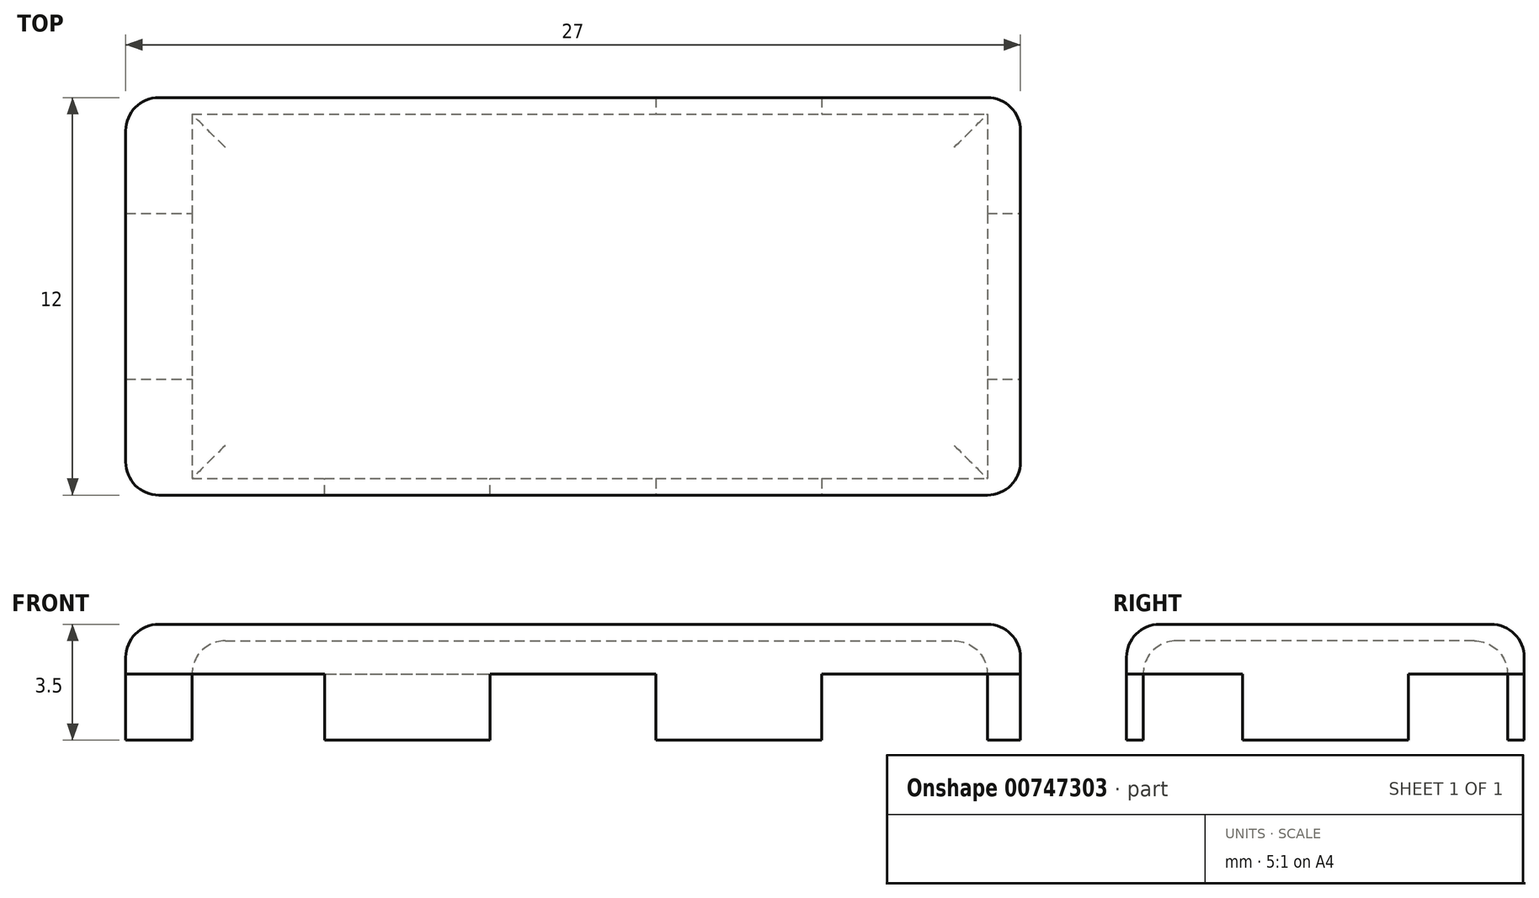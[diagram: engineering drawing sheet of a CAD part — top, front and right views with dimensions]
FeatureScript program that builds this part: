
annotation { "Feature Type Name" : "Feature", "Feature Type Description" : "" }
export const myFeature = defineFeature(function(context is Context, id is Id, definition is map)
    precondition{}
    {
        {
            var Q0;
            Q0=qCreatedBy(makeId("Top.planeOp"),FACE);
            var sketch = newSketch(context, id + "F0", { "sketchPlane" : qUnion([Q0])});
            skLineSegment(sketch, "E0.bottom", {"start": v(1, 0) * mm, "end": v(26, 0) * mm});
            skLineSegment(sketch, "E0.top", {"start": v(1, 12) * mm, "end": v(26, 12) * mm});
            skLineSegment(sketch, "E0.left", {"start": v(0, 1) * mm, "end": v(0, 11) * mm});
            skLineSegment(sketch, "E0.right", {"start": v(27, 1) * mm, "end": v(27, 11) * mm});
            skPoint(sketch, "E1.visualSharp", {"position": v(27, 12) * mm});
            skArc(sketch, "E1.filletArc", {"start": v(27, 11) * mm, "mid": v(26.7, 11.7) * mm, "end": v(26, 12) * mm});
            skPoint(sketch, "E2.visualSharp", {"position": v(27, 0) * mm});
            skArc(sketch, "E2.filletArc", {"start": v(26, 0) * mm, "mid": v(26.7, 0.3) * mm, "end": v(27, 1) * mm});
            skPoint(sketch, "E3.visualSharp", {"position": v(0, 0) * mm});
            skArc(sketch, "E3.filletArc", {"start": v(0, 1) * mm, "mid": v(0.3, 0.3) * mm, "end": v(1, 0) * mm});
            skPoint(sketch, "E4.visualSharp", {"position": v(0, 12) * mm});
            skArc(sketch, "E4.filletArc", {"start": v(1, 12) * mm, "mid": v(0.3, 11.7) * mm, "end": v(0, 11) * mm});
            skSolve(sketch);
        }
        {
            var Q0;
            Q0=makeQuery(id+"F0.imprint","IMPRINT",FACE,{"disambiguationData":[TD([[makeQuery(id+"F0.imprint","IMPRINT",EDGE,{"derivedFrom":sQuery(id+"F0.wireOp",EDGE,"E0.bottom")}),1.0]])]});
            extrude(context, id + "F1", {"entities" : qUnion([Q0]), "depth" : 1.5 * mm, "offsetDistance" : 25 * mm});
        }
        {
            var Q0;
            Q0=makeQuery(id+"F1.opExtrude","CAP_FACE",FACE,{"disambiguationData":[OSD([sQuery(id+"F0.wireOp",EDGE,"E0.bottom"),sQuery(id+"F0.wireOp",EDGE,"E0.top"),sQuery(id+"F0.wireOp",EDGE,"E0.left"),sQuery(id+"F0.wireOp",EDGE,"E0.right"),sQuery(id+"F0.wireOp",EDGE,"E1.filletArc"),sQuery(id+"F0.wireOp",EDGE,"E2.filletArc"),sQuery(id+"F0.wireOp",EDGE,"E3.filletArc"),sQuery(id+"F0.wireOp",EDGE,"E4.filletArc")])],"isStart":false});
            fillet(context, id + "F2", {"entities" : qUnion([Q0]), "radius" : 1 * mm, "tangentPropagation" : true, "allowEdgeOverflow" : false});
        }
        {
            var Q0;
            Q0=qCreatedBy(makeId("Top.planeOp"),FACE);
            var sketch = newSketch(context, id + "F3", { "sketchPlane" : qUnion([Q0])});
            skLineSegment(sketch, "E5.bottom", {"start": v(2, 11.5) * mm, "end": v(26, 11.5) * mm});
            skLineSegment(sketch, "E5.top", {"start": v(2, 0.5) * mm, "end": v(26, 0.5) * mm});
            skLineSegment(sketch, "E5.left", {"start": v(2, 11.5) * mm, "end": v(2, 0.5) * mm});
            skLineSegment(sketch, "E5.right", {"start": v(26, 11.5) * mm, "end": v(26, 0.5) * mm});
            skSolve(sketch);
        }
        {
            var Q0;
            Q0=qSketchRegion(id+"F3",true);
            extrude(context, id + "F4", {"entities" : qUnion([Q0]), "operationType" : NewBodyOperationType.REMOVE, "depth" : 1 * mm, "offsetDistance" : 25 * mm});
        }
        {
            var Q0;
            Q0=makeQuery(id+"F4.boolean.opBoolean","COPY",FACE,{"derivedFrom":makeQuery(id+"F4.opExtrude","CAP_FACE",FACE,{"disambiguationData":[OSD([sQuery(id+"F3.wireOp",EDGE,"E5.bottom"),sQuery(id+"F3.wireOp",EDGE,"E5.top"),sQuery(id+"F3.wireOp",EDGE,"E5.left"),sQuery(id+"F3.wireOp",EDGE,"E5.right")])],"isStart":false})});
            fillet(context, id + "F5", {"entities" : qUnion([Q0]), "radius" : 1 * mm, "tangentPropagation" : true, "allowEdgeOverflow" : false});
        }
        {
            var Q0;
            Q0=makeQuery(id+"F1.opExtrude","CAP_FACE",FACE,{"disambiguationData":[OSD([sQuery(id+"F0.wireOp",EDGE,"E0.bottom"),sQuery(id+"F0.wireOp",EDGE,"E0.top"),sQuery(id+"F0.wireOp",EDGE,"E0.left"),sQuery(id+"F0.wireOp",EDGE,"E0.right"),sQuery(id+"F0.wireOp",EDGE,"E1.filletArc"),sQuery(id+"F0.wireOp",EDGE,"E2.filletArc"),sQuery(id+"F0.wireOp",EDGE,"E3.filletArc"),sQuery(id+"F0.wireOp",EDGE,"E4.filletArc")])],"isStart":true});
            var sketch = newSketch(context, id + "F6", { "sketchPlane" : qUnion([Q0])});
            skLineSegment(sketch, "E6.bottom", {"start": v(0, -3.5) * mm, "end": v(2, -3.5) * mm});
            skLineSegment(sketch, "E6.top", {"start": v(0, -8.5) * mm, "end": v(2, -8.5) * mm});
            skLineSegment(sketch, "E6.left", {"start": v(0, -3.5) * mm, "end": v(0, -8.5) * mm});
            skLineSegment(sketch, "E6.right", {"start": v(2, -3.5) * mm, "end": v(2, -8.5) * mm});
            skLineSegment(sketch, "E7.bottom", {"start": v(26, -8.5) * mm, "end": v(27, -8.5) * mm});
            skLineSegment(sketch, "E7.top", {"start": v(26, -3.5) * mm, "end": v(27, -3.5) * mm});
            skLineSegment(sketch, "E7.left", {"start": v(26, -8.5) * mm, "end": v(26, -3.5) * mm});
            skLineSegment(sketch, "E7.right", {"start": v(27, -8.5) * mm, "end": v(27, -3.5) * mm});
            skLineSegment(sketch, "E8.bottom", {"start": v(6, 0) * mm, "end": v(11, 0) * mm});
            skLineSegment(sketch, "E8.top", {"start": v(6, -0.5) * mm, "end": v(11, -0.5) * mm});
            skLineSegment(sketch, "E8.left", {"start": v(6, 0) * mm, "end": v(6, -0.5) * mm});
            skLineSegment(sketch, "E8.right", {"start": v(11, 0) * mm, "end": v(11, -0.5) * mm});
            skLineSegment(sketch, "E9.bottom", {"start": v(16, -0.5) * mm, "end": v(21, -0.5) * mm});
            skLineSegment(sketch, "E9.top", {"start": v(16, 0) * mm, "end": v(21, 0) * mm});
            skLineSegment(sketch, "E9.left", {"start": v(16, -0.5) * mm, "end": v(16, 0) * mm});
            skLineSegment(sketch, "E9.right", {"start": v(21, -0.5) * mm, "end": v(21, 0) * mm});
            skLineSegment(sketch, "E10.bottom", {"start": v(21, -12) * mm, "end": v(16, -12) * mm});
            skLineSegment(sketch, "E10.top", {"start": v(21, -11.5) * mm, "end": v(16, -11.5) * mm});
            skLineSegment(sketch, "E10.left", {"start": v(21, -12) * mm, "end": v(21, -11.5) * mm});
            skLineSegment(sketch, "E10.right", {"start": v(16, -12) * mm, "end": v(16, -11.5) * mm});
            skSolve(sketch);
        }
        {
            var Q0;
            Q0=qSketchRegion(id+"F6",true);
            extrude(context, id + "F7", {"entities" : qUnion([Q0]), "operationType" : NewBodyOperationType.ADD, "depth" : 2 * mm, "offsetDistance" : 25 * mm});
        }
    });
